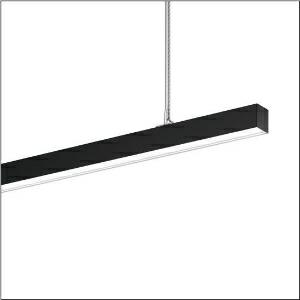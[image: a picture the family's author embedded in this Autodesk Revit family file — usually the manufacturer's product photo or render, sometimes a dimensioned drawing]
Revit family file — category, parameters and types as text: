
# Revit family: silica_r__21_51mx30tct9b_d278
name_source: partatom
category: Lighting Fixtures
units: mm (PartAtom-declared; Revit-internal decimal feet)

## family parameters
Cut with Voids When Loaded = No
Host = Face
Light Source = No
Part Type = Normal
Room Calculation Point = No
Round Connector Dimension = Use Diameter
Shared = No

## types (1)
- --- (1 x LED, 10300 lm, 84.4 W, 6500K)
    Apparent Load = 84 VA
    CIE Flux Codes = 47 79 96 58 100
    Color Rendering = 80
    Color Temperature = 6500K
    Default Elevation = 1800 mm
    Description = Silica® 21, office luminaire, primary optical cover: cover, of PMMA, opal, light emission: direct/indirect distribution, primary light characteristic: symmetric, installation type: suspended mounting, LED, rated luminous flux: 10.300lm, luminous efficacy: 116lm/W, light colour: 8tw, colour temperature: 2700..6500K, control gear: DALI DT8, with terminal, 3+2-pole, max. 2.5mm², mains connection: 220..240V, AC, 50/60Hz, rated input power: 88.7W, luminaire housing, of aluminium, matt jet black (RAL 9005), length: 3.004mm, width: 53mm, height: 53mm, protection rating (complete): IP20, insulation class (complete): insulation class I (protective earthing), certification: CE, permissible operating ambient temperature: 0..+35°C, standard: EN 50419, packaging unit: 1 piece
    Height = 53 mm
    Lamp = 1 x LED
    Lamp Light Flux = 10300 lm
    Lamp Power = 84.4 W
    Lamp count = 1
    Length = 3004 mm
    Luminous efficacy = 122 lm/W
    Manufacturer = Siteco
    ModVariant = No
    Model = 51MX30TCT9B
    Mounting Place = Ceiling
    Mounting Type = Pendant
    Number of Poles = 1
    OnlyDefault = Yes
    Power Factor = 1
    Product Name = Silica® 21
    Product group = office luminaire | ceiling pendant
    ProductGroupID = 904
    Protection Class = Protection class I
    Protection Degree = IP 20
    RLX_Detail_Level = 1
    RLX_Emergency_Light_Flux = 0 lm
    RLX_Emergency_Type = 0
    RLX_Emergency_Type_DB = No
    RlxData = <blob elided: 22781 chars, md5=eb9dc3f0>
    Socket = socket
    Standby Power = 0 W
    System Light Flux = 10300 lm
    System Power = 84 W
    Type Comments = individual setting
    Type Image = l_1335856.jpg
    URL = http://relux.com
    VarID = @adj_139626
    Voltage = 0 V
    Weight = 0.00 kg
    Width = 53 mm

## geometry (parser evidence)
native form markers: Blend x4, Sweep x12
no freeform markers — native parametric forms only
